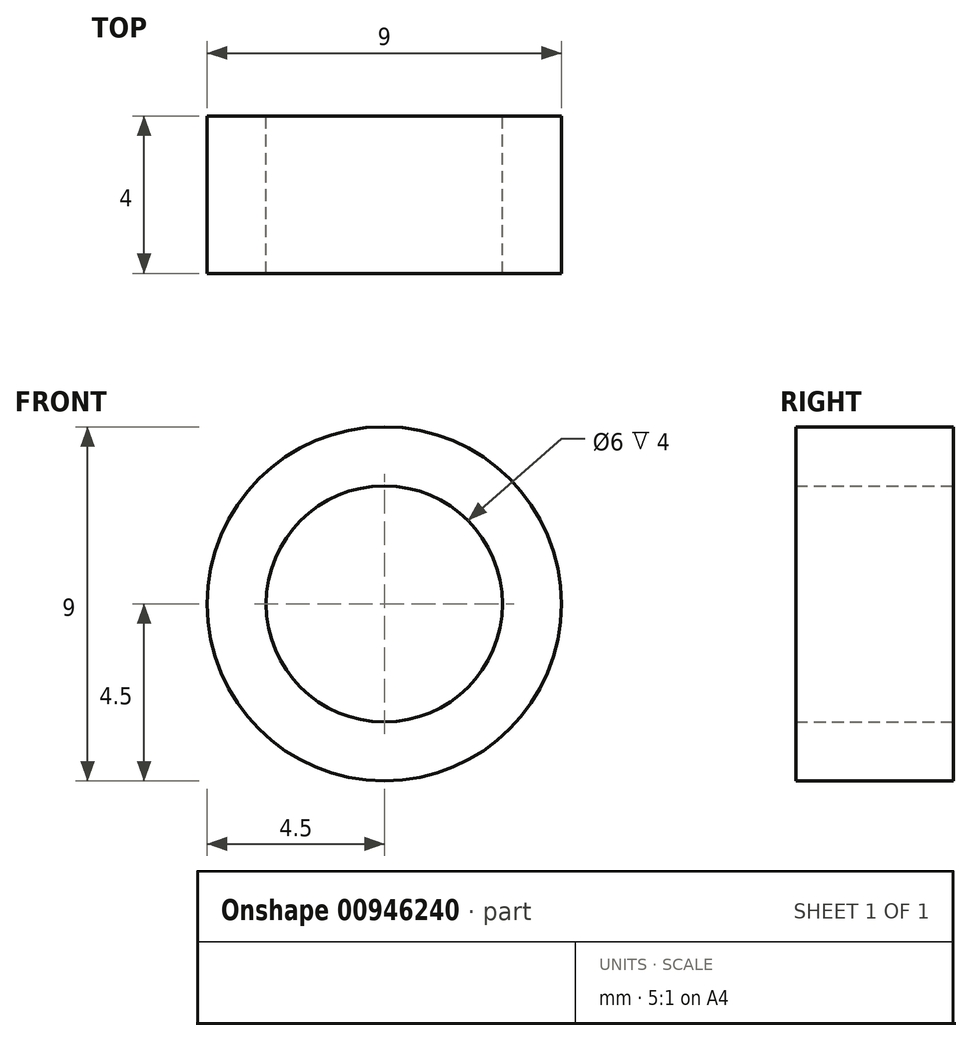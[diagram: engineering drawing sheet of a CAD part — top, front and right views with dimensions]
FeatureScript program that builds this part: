
annotation { "Feature Type Name" : "Feature", "Feature Type Description" : "" }
export const myFeature = defineFeature(function(context is Context, id is Id, definition is map)
    precondition{}
    {
        {
            var Q0;
            Q0=qCreatedBy(makeId("Front.planeOp"),FACE);
            var sketch = newSketch(context, id + "F0", { "sketchPlane" : qUnion([Q0])});
            skCircle(sketch, "E0", {"center": v(0, 0) * mm, "radius": 3 * mm});
            skCircle(sketch, "E1", {"center": v(0, 0) * mm, "radius": 4.5 * mm});
            skSolve(sketch);
        }
        {
            var Q0;
            Q0=makeQuery(id+"F0.imprint","IMPRINT",FACE,{"disambiguationData":[TD([[makeQuery(id+"F0.imprint","IMPRINT",EDGE,{"derivedFrom":sQuery(id+"F0.wireOp",EDGE,"E0")}),-1.0]])]});
            extrude(context, id + "F1", {"entities" : qUnion([Q0]), "depth" : 4 * mm, "offsetDistance" : 25.4 * mm});
        }
    });
